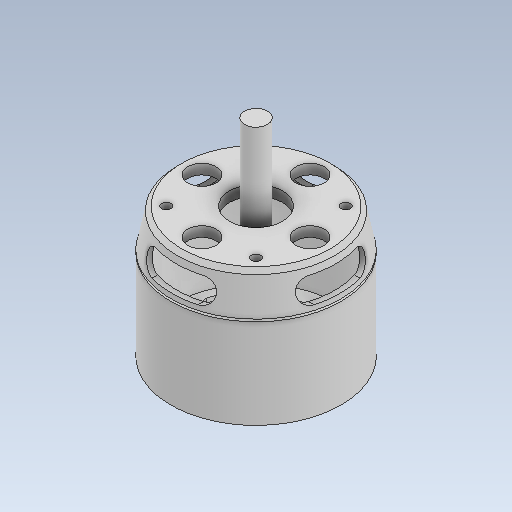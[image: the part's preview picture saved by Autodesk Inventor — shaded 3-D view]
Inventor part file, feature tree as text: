
AUTODESK INVENTOR PART (.ipt)
format: ipt  version: 2023 (Build 270158000, 158)  size: 339,968 bytes
history: native  units: in
note: dims shown in document units (in); Inventor stores cm internally (conversion verified against a paired STEP export)
features: sketch x4, other x3, plane x1
ambient origin geometry x8: Origin, YZ Plane, XZ Plane, XY Plane, X Axis, Y Axis, Z Axis, Center Point
bodies: Solid1 (feature_tree)
feature tree (8):
  other  "Drive Motor.ipt"
  other  "Solid1::Drive Motor.ipt"
  other  "TaggingFeature1"
  sketch  "Sketch1"  dims[d0=0.3937in]
  sketch  "Sketch2"
  sketch  "Sketch3"
  sketch  "Sketch4"
  plane  "Work Plane1"
